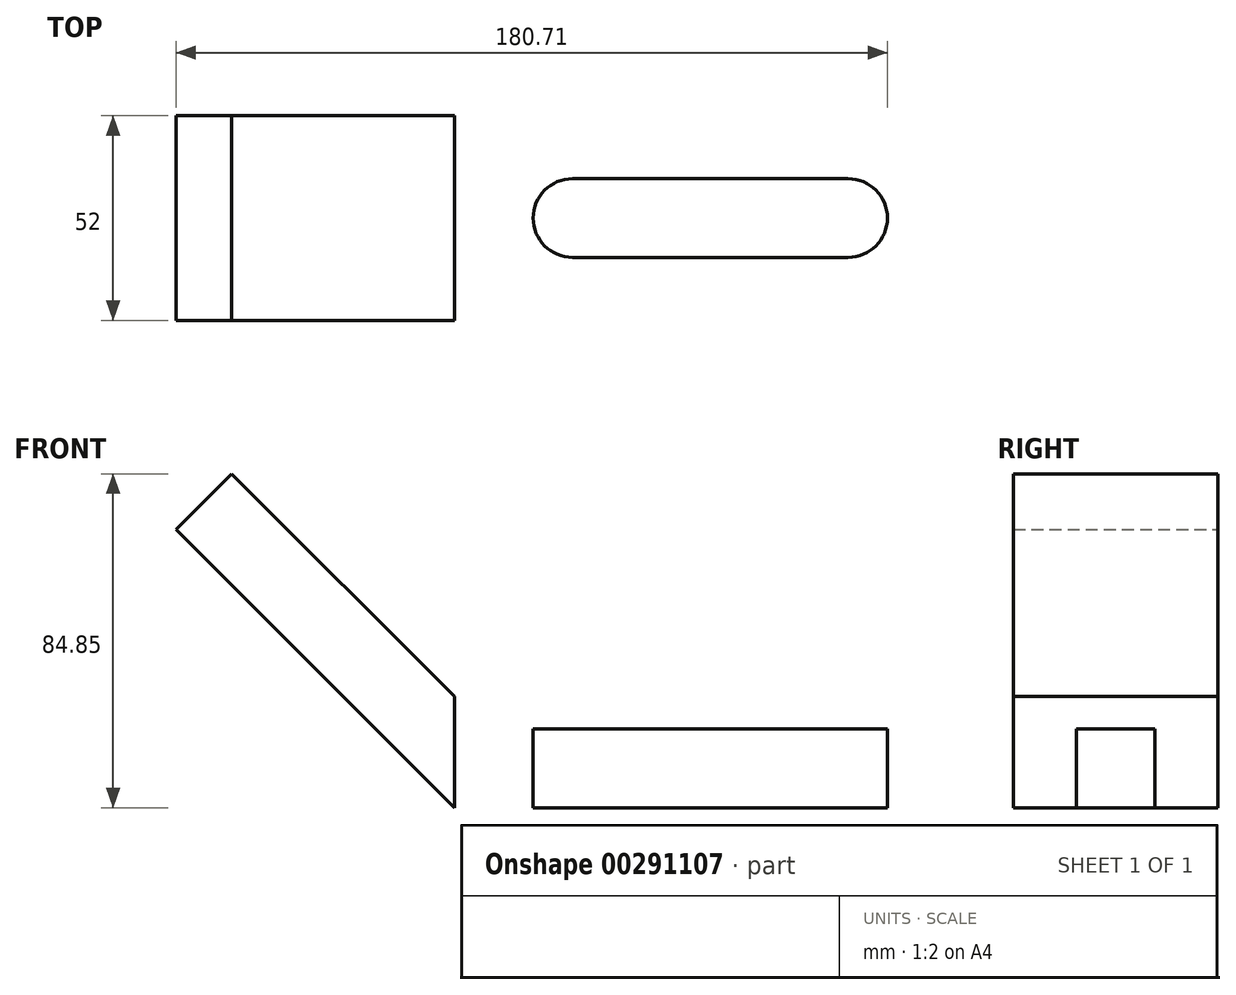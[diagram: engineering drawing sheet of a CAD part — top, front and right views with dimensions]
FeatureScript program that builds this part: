
annotation { "Feature Type Name" : "Feature", "Feature Type Description" : "" }
export const myFeature = defineFeature(function(context is Context, id is Id, definition is map)
    precondition{}
    {
        {
            var Q0;
            Q0=qCreatedBy(makeId("Front.planeOp"),FACE);
            var sketch = newSketch(context, id + "F0", { "sketchPlane" : qUnion([Q0])});
            skLineSegment(sketch, "E0.bottom", {"start": v(60, -10) * mm, "end": v(-60, -10) * mm});
            skLineSegment(sketch, "E0.top", {"start": v(60, 10) * mm, "end": v(-60, 10) * mm});
            skLineSegment(sketch, "E0.left", {"start": v(60, -10) * mm, "end": v(60, 10) * mm});
            skLineSegment(sketch, "E0.right", {"start": v(-60, -10) * mm, "end": v(-60, 10) * mm});
            skPoint(sketch, "E0.middle", {"position": v(0, 0) * mm});
            skLineSegment(sketch, "E1", {"start": v(-60, -10) * mm, "end": v(-130.71, 60.71) * mm});
            skLineSegment(sketch, "E2", {"start": v(-130.71, 60.71) * mm, "end": v(-116.57, 74.85) * mm});
            skLineSegment(sketch, "E3", {"start": v(-116.57, 74.85) * mm, "end": v(-51.72, 10) * mm});
            skSolve(sketch);
        }
        {
            var Q0;
            {var subQ0=sQuery(id+"F0.wireOp",EDGE,"E0.right");Q0=makeQuery(id+"F0.imprint","IMPRINT",FACE,{"disambiguationData":[TD([[makeQuery(id+"F0.imprint","IMPRINT",EDGE,{"derivedFrom":subQ0}),1.0]])]});}
            var Q1;
            Q1=makeQuery(id+"F0.imprint","IMPRINT",FACE,{"disambiguationData":[TD([[makeQuery(id+"F0.imprint","IMPRINT",EDGE,{"derivedFrom":sQuery(id+"F0.wireOp",EDGE,"E0.bottom")}),-1.0]])]});
            extrude(context, id + "F1", {"entities" : qUnion([Q0, Q1]), "depth" : 52 * mm});
        }
        {
            var Q0;
            Q0=makeQuery(id+"F1.opExtrude","SWEPT_FACE",FACE,{"disambiguationData":[OSD([sQuery(id+"F0.wireOp",EDGE,"E1")])]});
            var sketch = newSketch(context, id + "F2", { "sketchPlane" : qUnion([Q0])});
            skPoint(sketch, "E4.centerSnap0", {"position": v(-135.36, 26) * mm});
            skCircle(sketch, "E5", {"center": v(-109.36, 26) * mm, "radius": 26 * mm});
            skCircle(sketch, "E6", {"center": v(-109.36, 26) * mm, "radius": 10 * mm});
            skSolve(sketch);
        }
        {
            var Q0;
            Q0=makeQuery(id+"F2.imprint","IMPRINT",FACE,{"disambiguationData":[TD([[makeQuery(id+"F2.imprint","IMPRINT",EDGE,{"derivedFrom":sQuery(id+"F2.wireOp",EDGE,"E6")}),1.0]])]});
            var Q1;
            {var subQ0=sQuery(id+"F2.wireOp",EDGE,"E5");var subQ1=sQuery(id+"F0.wireOp",EDGE,"E1");var subQ4=makeQuery(id+"F1.opExtrude","CAP_EDGE",EDGE,{"disambiguationData":[OSD([subQ1])],"isStart":false});var subQ5=makeQuery(id+"F2.imprint","INTERSECT",VERTEX,{"derivedFrom":[subQ4,subQ0]});Q1=makeQuery(id+"F2.imprint","IMPRINT",FACE,{"disambiguationData":[TD([[makeQuery(id+"F2.imprint","IMPRINT",EDGE,{"disambiguationData":[TD([[subQ5,-1.0]])],"derivedFrom":subQ0}),-1.0]])]});}
            var Q2;
            {var subQ0=sQuery(id+"F2.wireOp",EDGE,"E5");var subQ1=sQuery(id+"F0.wireOp",EDGE,"E1");var subQ4=makeQuery(id+"F1.opExtrude","CAP_EDGE",EDGE,{"disambiguationData":[OSD([subQ1])],"isStart":true});var subQ5=makeQuery(id+"F2.imprint","INTERSECT",VERTEX,{"derivedFrom":[subQ4,subQ0]});Q2=makeQuery(id+"F2.imprint","IMPRINT",FACE,{"disambiguationData":[TD([[makeQuery(id+"F2.imprint","IMPRINT",EDGE,{"disambiguationData":[TD([[subQ5,1.0]])],"derivedFrom":subQ0}),-1.0]])]});}
            extrude(context, id + "F3", {"entities" : qUnion([Q0, Q1, Q2]), "operationType" : NewBodyOperationType.REMOVE, "endBound" : BoundingType.THROUGH_ALL, "oppositeDirection" : true, "depth" : 25 * mm});
        }
        {
            var Q0;
            Q0=makeQuery(id+"F1.opExtrude","SWEPT_FACE",FACE,{"disambiguationData":[OSD([sQuery(id+"F0.wireOp",EDGE,"E0.bottom")])]});
            var sketch = newSketch(context, id + "F4", { "sketchPlane" : qUnion([Q0])});
            skLineSegment(sketch, "E7", {"start": v(40, 26) * mm, "end": v(-30, 26) * mm});
            skPoint(sketch, "E7.startSnap0", {"position": v(60, 26) * mm});
            skArc(sketch, "E8.0.startCap", {"start": v(40, 36) * mm, "mid": v(50, 26) * mm, "end": v(40, 16) * mm});
            skArc(sketch, "E8.0.endCap", {"start": v(-30, 16) * mm, "mid": v(-40, 26) * mm, "end": v(-30, 36) * mm});
            skLineSegment(sketch, "E8.0.left", {"start": v(40, 16) * mm, "end": v(-30, 16) * mm});
            skLineSegment(sketch, "E8.0.right", {"start": v(40, 36) * mm, "end": v(-30, 36) * mm});
            skSolve(sketch);
        }
        {
            var Q0;
            Q0=makeQuery(id+"F4.imprint","IMPRINT",FACE,{"disambiguationData":[TD([[makeQuery(id+"F4.imprint","IMPRINT",EDGE,{"derivedFrom":sQuery(id+"F4.wireOp",EDGE,"E8.0.startCap")}),-1.0]])]});
            extrude(context, id + "F5", {"entities" : qUnion([Q0]), "operationType" : NewBodyOperationType.REMOVE, "endBound" : BoundingType.THROUGH_ALL, "oppositeDirection" : true, "depth" : 25 * mm});
        }
    });
